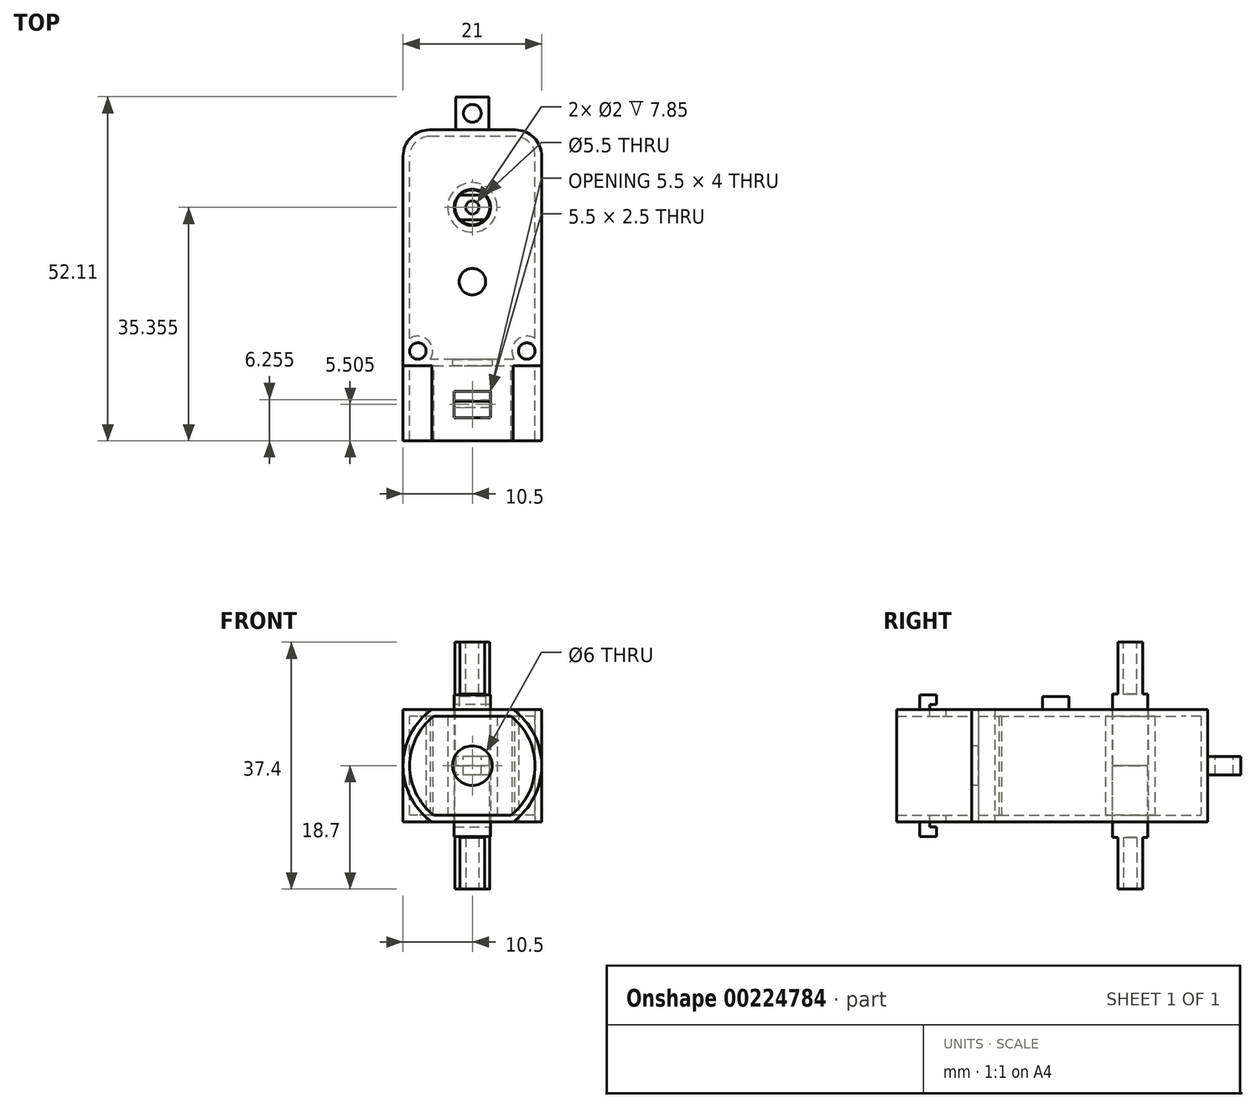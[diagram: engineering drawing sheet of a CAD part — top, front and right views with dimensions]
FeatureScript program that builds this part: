
annotation { "Feature Type Name" : "Feature", "Feature Type Description" : "" }
export const myFeature = defineFeature(function(context is Context, id is Id, definition is map)
    precondition{}
    {
        {
            var Q0;
            Q0=qCreatedBy(makeId("Top.planeOp"),FACE);
            var sketch = newSketch(context, id + "F0", { "sketchPlane" : qUnion([Q0])});
            skLineSegment(sketch, "E0.bottom", {"start": v(10.5, -17.88) * mm, "end": v(-10.5, -17.88) * mm});
            skLineSegment(sketch, "E0.top", {"start": v(10.5, 17.88) * mm, "end": v(-10.5, 17.88) * mm});
            skLineSegment(sketch, "E0.left", {"start": v(10.5, -17.88) * mm, "end": v(10.5, 17.88) * mm});
            skLineSegment(sketch, "E0.right", {"start": v(-10.5, -17.88) * mm, "end": v(-10.5, 17.88) * mm});
            skPoint(sketch, "E0.middle", {"position": v(0, 0) * mm});
            skCircle(sketch, "E1", {"center": v(0, 6.12) * mm, "radius": 2.75 * mm});
            skLineSegment(sketch, "E2", {"start": v(0, 8.88) * mm, "end": v(0, 17.88) * mm});
            skCircle(sketch, "E3", {"center": v(0, -5.13) * mm, "radius": 2 * mm});
            skLineSegment(sketch, "E4", {"start": v(0, 3.37) * mm, "end": v(0, -3.13) * mm});
            skCircle(sketch, "E5", {"center": v(-8.25, -15.63) * mm, "radius": 1.25 * mm});
            skLineSegment(sketch, "E6", {"start": v(-8.25, -16.88) * mm, "end": v(-8.25, -17.88) * mm});
            skLineSegment(sketch, "E7", {"start": v(-9.5, -15.63) * mm, "end": v(-10.5, -15.63) * mm});
            skLineSegment(sketch, "E8", {"start": v(0, -7.13) * mm, "end": v(0, -17.88) * mm});
            skCircle(sketch, "E9.MirrorC", {"center": v(8.25, -15.62) * mm, "radius": 1.25 * mm});
            skSolve(sketch);
        }
        {
            var Q0;
            {var subQ3=sQuery(id+"F0.wireOp",EDGE,"E2");Q0=makeQuery(id+"F0.imprint","IMPRINT",FACE,{"disambiguationData":[TD([[makeQuery(id+"F0.imprint","IMPRINT",EDGE,{"derivedFrom":subQ3}),1.0]])]});}
            var Q1;
            {var subQ3=sQuery(id+"F0.wireOp",EDGE,"E0.left");Q1=makeQuery(id+"F0.imprint","IMPRINT",FACE,{"disambiguationData":[TD([[makeQuery(id+"F0.imprint","IMPRINT",EDGE,{"derivedFrom":subQ3}),1.0]])]});}
            var Q2;
            {var subQ0=sQuery(id+"F0.wireOp",EDGE,"E6");Q2=makeQuery(id+"F0.imprint","IMPRINT",FACE,{"disambiguationData":[TD([[makeQuery(id+"F0.imprint","IMPRINT",EDGE,{"derivedFrom":subQ0}),-1.0]])]});}
            var Q3;
            {var subQ0=sQuery(id+"F0.wireOp",EDGE,"E3");var subQ1=makeQuery(id+"F0.imprint","INTERSECT",VERTEX,{"derivedFrom":[subQ0,sQuery(id+"F0.wireOp",EDGE,"E4")]});Q3=makeQuery(id+"F0.imprint","IMPRINT",FACE,{"disambiguationData":[TD([[makeQuery(id+"F0.imprint","IMPRINT",EDGE,{"disambiguationData":[TD([[subQ1,-1.0]])],"derivedFrom":subQ0}),1.0]])]});}
            extrude(context, id + "F1", {"entities" : qUnion([Q0, Q1, Q2, Q3]), "depth" : 17 * mm, "symmetric" : true});
        }
        {
            var Q0;
            Q0=makeQuery(id+"F1.opExtrude","SWEPT_EDGE",EDGE,{"disambiguationData":[OSD([sQuery(id+"F0.wireOp",EDGE,"E0.top"),sQuery(id+"F0.wireOp",EDGE,"E0.right")])]});
            var Q1;
            Q1=makeQuery(id+"F1.opExtrude","SWEPT_EDGE",EDGE,{"disambiguationData":[OSD([sQuery(id+"F0.wireOp",EDGE,"E0.top"),sQuery(id+"F0.wireOp",EDGE,"E0.left")])]});
            fillet(context, id + "F2", {"entities" : qUnion([Q0, Q1]), "radius" : 4 * mm, "tangentPropagation" : true, "allowEdgeOverflow" : false});
        }
        {
            var Q0;
            Q0=makeQuery(id+"F1.opExtrude","SWEPT_FACE",FACE,{"disambiguationData":[OSD([sQuery(id+"F0.wireOp",EDGE,"E1")])]});
            var Q1;
            Q1=makeQuery(id+"F1.opExtrude","SWEPT_BODY",BODY,{"disambiguationData":[OSD([sQuery(id+"F0.wireOp",EDGE,"E0.bottom"),sQuery(id+"F0.wireOp",EDGE,"E0.top"),sQuery(id+"F0.wireOp",EDGE,"E0.left"),sQuery(id+"F0.wireOp",EDGE,"E0.right"),sQuery(id+"F0.wireOp",EDGE,"E1"),sQuery(id+"F0.wireOp",EDGE,"E3"),sQuery(id+"F0.wireOp",EDGE,"E5"),sQuery(id+"F0.wireOp",EDGE,"E9.MirrorC")])]});
            shell(context, id + "F3", {"isHollow" : true, "entities" : qUnion([Q0]), "parts" : qUnion([Q1]), "thickness" : 1 * mm});
        }
        {
            var Q0;
            Q0=makeQuery(id+"F1.opExtrude","SWEPT_FACE",FACE,{"disambiguationData":[OSD([sQuery(id+"F0.wireOp",EDGE,"E0.top")])]});
            var sketch = newSketch(context, id + "F4", { "sketchPlane" : qUnion([Q0])});
            skLineSegment(sketch, "E10.bottom", {"start": v(-2.5, 1.4) * mm, "end": v(2.5, 1.4) * mm});
            skLineSegment(sketch, "E10.top", {"start": v(-2.5, -1.4) * mm, "end": v(2.5, -1.4) * mm});
            skLineSegment(sketch, "E10.left", {"start": v(-2.5, 1.4) * mm, "end": v(-2.5, -1.4) * mm});
            skLineSegment(sketch, "E10.right", {"start": v(2.5, 1.4) * mm, "end": v(2.5, -1.4) * mm});
            skPoint(sketch, "E10.middle", {"position": v(0, 0) * mm});
            skSolve(sketch);
        }
        {
            var Q0;
            Q0 = qSketchRegion(id + "F4", true);
            extrude(context, id + "F5", {"entities" : qUnion([Q0]), "operationType" : NewBodyOperationType.ADD, "depth" : 5 * mm});
        }
        {
            var Q0;
            Q0=makeQuery(id+"F5.opExtrude","CAP_EDGE",EDGE,{"disambiguationData":[OSD([sQuery(id+"F4.wireOp",EDGE,"E10.right")])],"isStart":false});
            var Q1;
            Q1=makeQuery(id+"F5.opExtrude","CAP_EDGE",EDGE,{"disambiguationData":[OSD([sQuery(id+"F4.wireOp",EDGE,"E10.left")])],"isStart":false});
            var Q2;
            Q2=makeQuery(id+"F5.opExtrude","CAP_EDGE",EDGE,{"disambiguationData":[OSD([sQuery(id+"F4.wireOp",EDGE,"E10.left")])],"isStart":true});
            var Q3;
            Q3=makeQuery(id+"F5.opExtrude","CAP_EDGE",EDGE,{"disambiguationData":[OSD([sQuery(id+"F4.wireOp",EDGE,"E10.right")])],"isStart":true});
            fillet(context, id + "F6", {"entities" : qUnion([Q0, Q1, Q2, Q3]), "radius" : (1 / 8) * mm, "tangentPropagation" : true, "allowEdgeOverflow" : false});
        }
        {
            var Q0;
            Q0=makeQuery(id+"F5.opExtrude","SWEPT_FACE",FACE,{"disambiguationData":[OSD([sQuery(id+"F4.wireOp",EDGE,"E10.bottom")])]});
            var sketch = newSketch(context, id + "F7", { "sketchPlane" : qUnion([Q0])});
            skCircle(sketch, "E11", {"center": v(0, 20.38) * mm, "radius": 1.35 * mm});
            skPoint(sketch, "E11.centerSnap0", {"position": v(-2.5, 20.38) * mm});
            skSolve(sketch);
        }
        {
            var Q0;
            Q0 = qSketchRegion(id + "F7", true);
            extrude(context, id + "F8", {"entities" : qUnion([Q0]), "operationType" : NewBodyOperationType.REMOVE, "oppositeDirection" : true, "depth" : 2.8 * mm});
        }
        {
            var Q0;
            Q0=makeQuery(id+"F1.opExtrude","SWEPT_FACE",FACE,{"disambiguationData":[OSD([sQuery(id+"F0.wireOp",EDGE,"E0.bottom")])]});
            var sketch = newSketch(context, id + "F9", { "sketchPlane" : qUnion([Q0])});
            skArc(sketch, "E12", {"start": v(-6.16, 8.5) * mm, "mid": v(-10.5, 0) * mm, "end": v(-6.16, -8.5) * mm});
            skLineSegment(sketch, "E13", {"start": v(-6.16, 8.5) * mm, "end": v(6.16, 8.5) * mm});
            skLineSegment(sketch, "E14", {"start": v(-6.16, -8.5) * mm, "end": v(6.16, -8.5) * mm});
            skArc(sketch, "E15.trimOffspring", {"start": v(6.16, -8.5) * mm, "mid": v(10.5, 0) * mm, "end": v(6.16, 8.5) * mm});
            skArc(sketch, "E16", {"start": v(4.24, -8.5) * mm, "mid": v(9.5, 0) * mm, "end": v(4.24, 8.5) * mm});
            skLineSegment(sketch, "E17", {"start": v(-4.24, 8.5) * mm, "end": v(4.24, 8.5) * mm});
            skLineSegment(sketch, "E18", {"start": v(-4.24, -8.5) * mm, "end": v(4.24, -8.5) * mm});
            skArc(sketch, "E19.trimOffspring", {"start": v(-4.24, 8.5) * mm, "mid": v(-9.5, 0) * mm, "end": v(-4.24, -8.5) * mm});
            skLineSegment(sketch, "E20", {"start": v(-5.83, 7.5) * mm, "end": v(5.83, 7.5) * mm});
            skLineSegment(sketch, "E21", {"start": v(-5.83, -7.5) * mm, "end": v(5.83, -7.5) * mm});
            skLineSegment(sketch, "E22", {"start": v(-1.98, -7.5) * mm, "end": v(-1.98, -8.5) * mm});
            skLineSegment(sketch, "E23", {"start": v(-2.47, 7.5) * mm, "end": v(-2.47, 8.5) * mm});
            skSolve(sketch);
        }
        {
            var Q0;
            Q0 = qSketchRegion(id + "F9", true);
            extrude(context, id + "F10", {"entities" : qUnion([Q0]), "operationType" : NewBodyOperationType.ADD, "depth" : 11.35 * mm});
        }
        {
            var Q0;
            Q0=makeQuery(id+"F10.boolean.opBoolean","SPLIT",FACE,{"disambiguationData":[TD([makeQuery(id+"F10.opExtrude","SWEPT_FACE",FACE,{"disambiguationData":[OSD([sQuery(id+"F9.wireOp",EDGE,"E16")])]}),makeQuery(id+"F10.opExtrude","SWEPT_FACE",FACE,{"disambiguationData":[OSD([sQuery(id+"F9.wireOp",EDGE,"E19.trimOffspring")])]}),makeQuery(id+"F10.opExtrude","SWEPT_FACE",FACE,{"disambiguationData":[OSD([sQuery(id+"F9.wireOp",EDGE,"E20")])]}),makeQuery(id+"F10.opExtrude","SWEPT_FACE",FACE,{"disambiguationData":[OSD([sQuery(id+"F9.wireOp",EDGE,"E21")])]})])],"derivedFrom":makeQuery(id+"F1.opExtrude","SWEPT_FACE",FACE,{"disambiguationData":[OSD([sQuery(id+"F0.wireOp",EDGE,"E0.bottom")])]})});
            var sketch = newSketch(context, id + "F11", { "sketchPlane" : qUnion([Q0])});
            skCircle(sketch, "E24", {"center": v(0, 0) * mm, "radius": 3 * mm});
            skSolve(sketch);
        }
        {
            var Q0;
            Q0 = qSketchRegion(id + "F11", true);
            extrude(context, id + "F12", {"entities" : qUnion([Q0]), "operationType" : NewBodyOperationType.REMOVE, "oppositeDirection" : true, "depth" : 1 * mm});
        }
        {
            var Q0;
            Q0=makeQuery(id+"F10.boolean.opBoolean","MERGE",FACE,{"derivedFrom":[makeQuery(id+"F1.opExtrude","CAP_FACE",FACE,{"disambiguationData":[OSD([sQuery(id+"F0.wireOp",EDGE,"E0.bottom"),sQuery(id+"F0.wireOp",EDGE,"E0.top"),sQuery(id+"F0.wireOp",EDGE,"E0.left"),sQuery(id+"F0.wireOp",EDGE,"E0.right"),sQuery(id+"F0.wireOp",EDGE,"E1"),sQuery(id+"F0.wireOp",EDGE,"E5"),sQuery(id+"F0.wireOp",EDGE,"E9.MirrorC")])],"isStart":false}),makeQuery(id+"F10.opExtrude","SWEPT_FACE",FACE,{"disambiguationData":[OSD([sQuery(id+"F9.wireOp",EDGE,"E13"),sQuery(id+"F9.wireOp",EDGE,"E17")])]})]});
            var sketch = newSketch(context, id + "F13", { "sketchPlane" : qUnion([Q0])});
            skPoint(sketch, "E25.0", {"position": v(0, -5.13) * mm});
            skCircle(sketch, "E26.0", {"center": v(0, -5.13) * mm, "radius": 2 * mm});
            skSolve(sketch);
        }
        {
            var Q0;
            Q0=makeQuery(id+"F13.imprint","IMPRINT",FACE,{"disambiguationData":[TD([[makeQuery(id+"F13.imprint","IMPRINT",EDGE,{"derivedFrom":sQuery(id+"F13.wireOp",EDGE,"E26.0")}),1.0]])]});
            extrude(context, id + "F14", {"entities" : qUnion([Q0]), "operationType" : NewBodyOperationType.ADD, "depth" : 2 * mm});
        }
        {
            var Q0;
            Q0=makeQuery(id+"F10.boolean.opBoolean","MERGE",FACE,{"derivedFrom":[makeQuery(id+"F1.opExtrude","CAP_FACE",FACE,{"disambiguationData":[OSD([sQuery(id+"F0.wireOp",EDGE,"E0.bottom"),sQuery(id+"F0.wireOp",EDGE,"E0.top"),sQuery(id+"F0.wireOp",EDGE,"E0.left"),sQuery(id+"F0.wireOp",EDGE,"E0.right"),sQuery(id+"F0.wireOp",EDGE,"E1"),sQuery(id+"F0.wireOp",EDGE,"E5"),sQuery(id+"F0.wireOp",EDGE,"E9.MirrorC")])],"isStart":false}),makeQuery(id+"F10.opExtrude","SWEPT_FACE",FACE,{"disambiguationData":[OSD([sQuery(id+"F9.wireOp",EDGE,"E13"),sQuery(id+"F9.wireOp",EDGE,"E17")])]})]});
            var sketch = newSketch(context, id + "F15", { "sketchPlane" : qUnion([Q0])});
            skLineSegment(sketch, "E27.bottom", {"start": v(2.75, -24.23) * mm, "end": v(-2.75, -24.23) * mm});
            skLineSegment(sketch, "E27.top", {"start": v(2.75, -21.73) * mm, "end": v(-2.75, -21.73) * mm});
            skLineSegment(sketch, "E27.left", {"start": v(2.75, -24.23) * mm, "end": v(2.75, -21.73) * mm});
            skLineSegment(sketch, "E27.right", {"start": v(-2.75, -24.23) * mm, "end": v(-2.75, -21.73) * mm});
            skPoint(sketch, "E27.middle", {"position": v(0, -22.98) * mm});
            skPoint(sketch, "E27.middle.positionSnap0", {"position": v(0, -29.23) * mm});
            skPoint(sketch, "E27.centerSnap0", {"position": v(0, -29.23) * mm});
            skLineSegment(sketch, "E28", {"start": v(-1.5, -24.23) * mm, "end": v(-1.5, -29.23) * mm});
            skSolve(sketch);
        }
        {
            var Q0;
            Q0 = qSketchRegion(id + "F15", true);
            extrude(context, id + "F16", {"entities" : qUnion([Q0]), "operationType" : NewBodyOperationType.REMOVE, "oppositeDirection" : true, "depth" : 25 * mm});
        }
        {
            var Q0;
            Q0=makeQuery(id+"F10.boolean.opBoolean","MERGE",FACE,{"derivedFrom":[makeQuery(id+"F1.opExtrude","CAP_FACE",FACE,{"disambiguationData":[OSD([sQuery(id+"F0.wireOp",EDGE,"E0.bottom"),sQuery(id+"F0.wireOp",EDGE,"E0.top"),sQuery(id+"F0.wireOp",EDGE,"E0.left"),sQuery(id+"F0.wireOp",EDGE,"E0.right"),sQuery(id+"F0.wireOp",EDGE,"E1"),sQuery(id+"F0.wireOp",EDGE,"E5"),sQuery(id+"F0.wireOp",EDGE,"E9.MirrorC")])],"isStart":false}),makeQuery(id+"F10.opExtrude","SWEPT_FACE",FACE,{"disambiguationData":[OSD([sQuery(id+"F9.wireOp",EDGE,"E13"),sQuery(id+"F9.wireOp",EDGE,"E17")])]})]});
            var sketch = newSketch(context, id + "F17", { "sketchPlane" : qUnion([Q0])});
            skPoint(sketch, "E29.0", {"position": v(2.75, -24.23) * mm});
            skLineSegment(sketch, "E30.bottom", {"start": v(-2.75, -24.23) * mm, "end": v(2.75, -24.23) * mm});
            skLineSegment(sketch, "E30.top", {"start": v(-2.75, -25.73) * mm, "end": v(2.75, -25.73) * mm});
            skLineSegment(sketch, "E30.left", {"start": v(-2.75, -24.23) * mm, "end": v(-2.75, -25.73) * mm});
            skLineSegment(sketch, "E30.right", {"start": v(2.75, -24.23) * mm, "end": v(2.75, -25.73) * mm});
            skSolve(sketch);
        }
        {
            var Q0;
            Q0 = qSketchRegion(id + "F17", true);
            extrude(context, id + "F18", {"entities" : qUnion([Q0]), "operationType" : NewBodyOperationType.ADD, "depth" : 2.25 * mm});
        }
        {
            var Q0;
            Q0=makeQuery(id+"F18.opExtrude","SWEPT_FACE",FACE,{"disambiguationData":[OSD([sQuery(id+"F17.wireOp",EDGE,"E30.top")])]});
            var sketch = newSketch(context, id + "F19", { "sketchPlane" : qUnion([Q0])});
            skLineSegment(sketch, "E31.bottom", {"start": v(-2.75, 10.75) * mm, "end": v(2.75, 10.75) * mm});
            skLineSegment(sketch, "E31.top", {"start": v(-2.75, 9.25) * mm, "end": v(2.75, 9.25) * mm});
            skLineSegment(sketch, "E31.left", {"start": v(-2.75, 10.75) * mm, "end": v(-2.75, 9.25) * mm});
            skLineSegment(sketch, "E31.right", {"start": v(2.75, 10.75) * mm, "end": v(2.75, 9.25) * mm});
            skSolve(sketch);
        }
        {
            var Q0;
            Q0 = qSketchRegion(id + "F19", true);
            extrude(context, id + "F20", {"entities" : qUnion([Q0]), "operationType" : NewBodyOperationType.ADD, "oppositeDirection" : true, "depth" : 2.5 * mm});
        }
        {
            var Q0;
            Q0=makeQuery(id+"F10.boolean.opBoolean","MERGE",FACE,{"derivedFrom":[makeQuery(id+"F1.opExtrude","CAP_FACE",FACE,{"disambiguationData":[OSD([sQuery(id+"F0.wireOp",EDGE,"E0.bottom"),sQuery(id+"F0.wireOp",EDGE,"E0.top"),sQuery(id+"F0.wireOp",EDGE,"E0.left"),sQuery(id+"F0.wireOp",EDGE,"E0.right"),sQuery(id+"F0.wireOp",EDGE,"E1"),sQuery(id+"F0.wireOp",EDGE,"E5"),sQuery(id+"F0.wireOp",EDGE,"E9.MirrorC")])],"isStart":true}),makeQuery(id+"F10.opExtrude","SWEPT_FACE",FACE,{"disambiguationData":[OSD([sQuery(id+"F9.wireOp",EDGE,"E14"),sQuery(id+"F9.wireOp",EDGE,"E18")])]})]});
            var sketch = newSketch(context, id + "F21", { "sketchPlane" : qUnion([Q0])});
            skLineSegment(sketch, "E32.bottom", {"start": v(2.75, 24.23) * mm, "end": v(-2.75, 24.23) * mm});
            skLineSegment(sketch, "E32.top", {"start": v(2.75, 25.73) * mm, "end": v(-2.75, 25.73) * mm});
            skLineSegment(sketch, "E32.left", {"start": v(2.75, 24.23) * mm, "end": v(2.75, 25.73) * mm});
            skLineSegment(sketch, "E32.right", {"start": v(-2.75, 24.23) * mm, "end": v(-2.75, 25.73) * mm});
            skSolve(sketch);
        }
        {
            var Q0;
            Q0 = qSketchRegion(id + "F21", true);
            extrude(context, id + "F22", {"entities" : qUnion([Q0]), "operationType" : NewBodyOperationType.ADD, "depth" : 2.25 * mm});
        }
        {
            var Q0;
            Q0=makeQuery(id+"F22.boolean.opBoolean","MERGE",FACE,{"derivedFrom":[makeQuery(id+"F16.boolean.opBoolean","COPY",FACE,{"disambiguationData":[TD([makeQuery(id+"F10.opExtrude","SWEPT_FACE",FACE,{"disambiguationData":[OSD([sQuery(id+"F9.wireOp",EDGE,"E21")])]})])],"derivedFrom":makeQuery(id+"F16.opExtrude","SWEPT_FACE",FACE,{"disambiguationData":[OSD([sQuery(id+"F15.wireOp",EDGE,"E27.bottom")])]})}),makeQuery(id+"F22.opExtrude","SWEPT_FACE",FACE,{"disambiguationData":[OSD([sQuery(id+"F21.wireOp",EDGE,"E32.bottom")])]})]});
            var sketch = newSketch(context, id + "F23", { "sketchPlane" : qUnion([Q0])});
            skLineSegment(sketch, "E33.bottom", {"start": v(2.75, -10.75) * mm, "end": v(-2.75, -10.75) * mm});
            skLineSegment(sketch, "E33.top", {"start": v(2.75, -9.25) * mm, "end": v(-2.75, -9.25) * mm});
            skLineSegment(sketch, "E33.left", {"start": v(2.75, -10.75) * mm, "end": v(2.75, -9.25) * mm});
            skLineSegment(sketch, "E33.right", {"start": v(-2.75, -10.75) * mm, "end": v(-2.75, -9.25) * mm});
            skSolve(sketch);
        }
        {
            var Q0;
            Q0 = qSketchRegion(id + "F23", true);
            extrude(context, id + "F24", {"entities" : qUnion([Q0]), "operationType" : NewBodyOperationType.ADD, "depth" : 1 * mm});
        }
        {
            var Q0;
            {var subQ3=sQuery(id+"F0.wireOp",EDGE,"E0.left");Q0=makeQuery(id+"F0.imprint","IMPRINT",FACE,{"disambiguationData":[TD([[makeQuery(id+"F0.imprint","IMPRINT",EDGE,{"derivedFrom":subQ3}),1.0]])]});}
            var sketch = newSketch(context, id + "F25", { "sketchPlane" : qUnion([Q0])});
            skCircle(sketch, "E34.0", {"center": v(0, 6.12) * mm, "radius": 2.75 * mm, "construction": true});
            skCircle(sketch, "E35", {"center": v(0, 6.12) * mm, "radius": 2.64 * mm});
            skSolve(sketch);
        }
        {
            var Q0;
            Q0 = qSketchRegion(id + "F25", true);
            extrude(context, id + "F26", {"entities" : qUnion([Q0]), "depth" : (37.4 / 2) * mm});
        }
        {
            var Q0;
            Q0=makeQuery(id+"F26.opExtrude","CAP_FACE",FACE,{"disambiguationData":[OSD([sQuery(id+"F25.wireOp",EDGE,"E35")])],"isStart":false});
            var sketch = newSketch(context, id + "F27", { "sketchPlane" : qUnion([Q0])});
            skLineSegment(sketch, "E36", {"start": v(-1.86, 4.25) * mm, "end": v(1.86, 4.25) * mm});
            skLineSegment(sketch, "E37", {"start": v(0, 6.12) * mm, "end": v(-1.71, 6.12) * mm, "construction": true});
            skLineSegment(sketch, "E38.MirrorCS", {"start": v(-1.86, 8) * mm, "end": v(1.86, 8) * mm});
            skCircle(sketch, "E39.0", {"center": v(0, 6.12) * mm, "radius": 2.64 * mm});
            skPoint(sketch, "E40.orphan", {"position": v(-2.7, 4.25) * mm});
            skPoint(sketch, "E41.orphan", {"position": v(-2.7, 8) * mm});
            skPoint(sketch, "E42.orphan", {"position": v(2.7, 8) * mm});
            skPoint(sketch, "E43.orphan", {"position": v(2.7, 4.25) * mm});
            skCircle(sketch, "E44", {"center": v(0, 6.12) * mm, "radius": 1 * mm});
            skSolve(sketch);
        }
        {
            var Q0;
            {var subQ0=sQuery(id+"F27.wireOp",EDGE,"E36");Q0=makeQuery(id+"F27.imprint","IMPRINT",FACE,{"disambiguationData":[TD([[makeQuery(id+"F27.imprint","IMPRINT",EDGE,{"derivedFrom":subQ0}),-1.0]])]});}
            var Q1;
            {var subQ0=sQuery(id+"F27.wireOp",EDGE,"E38.MirrorCS");Q1=makeQuery(id+"F27.imprint","IMPRINT",FACE,{"disambiguationData":[TD([[makeQuery(id+"F27.imprint","IMPRINT",EDGE,{"derivedFrom":subQ0}),1.0]])]});}
            var Q2;
            Q2=makeQuery(id+"F27.imprint","IMPRINT",FACE,{"disambiguationData":[TD([[makeQuery(id+"F27.imprint","IMPRINT",EDGE,{"derivedFrom":sQuery(id+"F27.wireOp",EDGE,"E44")}),1.0]])]});
            extrude(context, id + "F28", {"entities" : qUnion([Q0, Q1, Q2]), "operationType" : NewBodyOperationType.REMOVE, "oppositeDirection" : true, "depth" : 7.85 * mm});
        }
        {
            var Q0;
            Q0=makeQuery(id+"F26.opExtrude","SWEPT_BODY",BODY,{"disambiguationData":[OSD([sQuery(id+"F25.wireOp",EDGE,"E35")])]});
            var Q1;
            Q1=qCreatedBy(makeId("Top.planeOp"),FACE);
            mirror(context, id + "F29", {"operationType" : NewBodyOperationType.ADD, "entities" : qUnion([Q0]), "mirrorPlane" : qUnion([Q1])});
        }
    });
